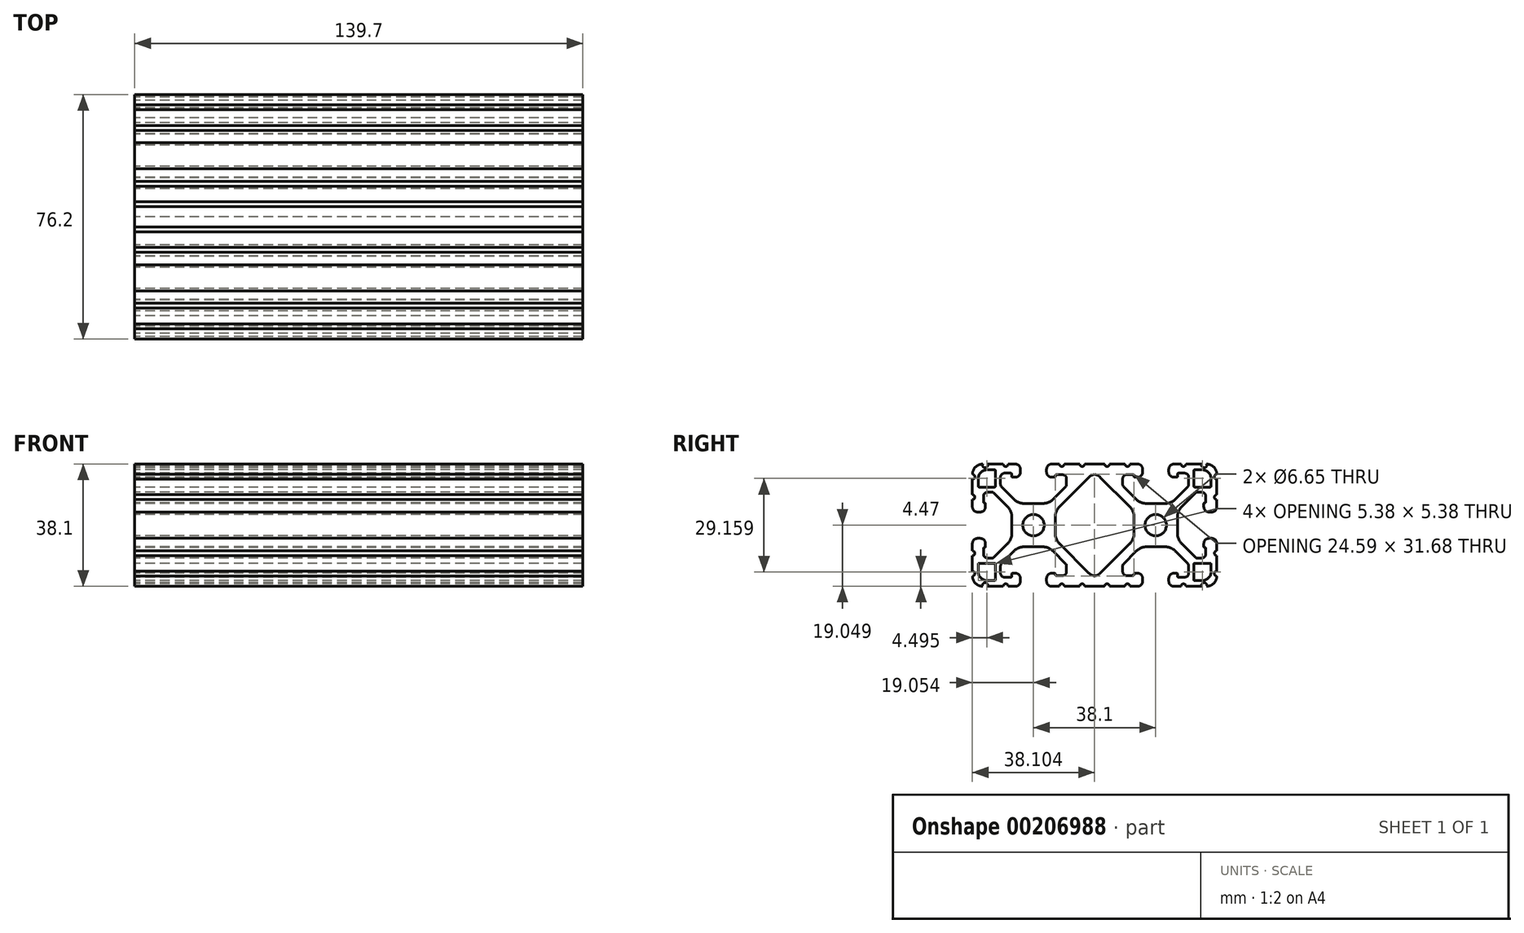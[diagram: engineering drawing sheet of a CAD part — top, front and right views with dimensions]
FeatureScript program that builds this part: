
annotation { "Feature Type Name" : "Feature", "Feature Type Description" : "" }
export const myFeature = defineFeature(function(context is Context, id is Id, definition is map)
    precondition{}
    {
        {
            var Q0;
            Q0=qCreatedBy(makeId("Right.planeOp"),FACE);
            var sketch = newSketch(context, id + "F0", { "sketchPlane" : qUnion([Q0])});
            skArc(sketch, "E0.0.0", {"start": v(-2.87, 19.05) * mm, "mid": v(-3.63, 18.29) * mm, "end": v(-4.4, 19.05) * mm});
            skLineSegment(sketch, "E0.0.1", {"start": v(-4.4, 19.05) * mm, "end": v(-9.22, 19.05) * mm});
            skArc(sketch, "E0.0.2", {"start": v(-9.22, 19.05) * mm, "mid": v(-9.98, 18.29) * mm, "end": v(-10.74, 19.05) * mm});
            skLineSegment(sketch, "E0.0.3", {"start": v(-10.74, 19.05) * mm, "end": v(-13.16, 19.05) * mm});
            skArc(sketch, "E0.0.4", {"start": v(-13.16, 19.05) * mm, "mid": v(-14.27, 18.59) * mm, "end": v(-14.73, 17.47) * mm});
            skLineSegment(sketch, "E0.0.5", {"start": v(-14.73, 17.47) * mm, "end": v(-14.73, 16.56) * mm});
            skArc(sketch, "E0.0.6", {"start": v(-14.73, 16.56) * mm, "mid": v(-14.27, 15.45) * mm, "end": v(-13.16, 14.99) * mm});
            skLineSegment(sketch, "E0.0.7", {"start": v(-13.16, 14.99) * mm, "end": v(-12.22, 14.99) * mm});
            skArc(sketch, "E0.0.8", {"start": v(-12.22, 14.99) * mm, "mid": v(-12.04, 15.06) * mm, "end": v(-11.96, 15.24) * mm});
            skLineSegment(sketch, "E0.0.9", {"start": v(-11.96, 15.24) * mm, "end": v(-11.96, 15.5) * mm});
            skArc(sketch, "E0.0.10", {"start": v(-11.96, 15.5) * mm, "mid": v(-11.89, 15.68) * mm, "end": v(-11.7, 15.75) * mm});
            skLineSegment(sketch, "E0.0.11", {"start": v(-11.7, 15.75) * mm, "end": v(-9.78, 15.75) * mm});
            skArc(sketch, "E0.0.12", {"start": v(-9.78, 15.75) * mm, "mid": v(-8.88, 15.38) * mm, "end": v(-8.5, 14.48) * mm});
            skLineSegment(sketch, "E0.0.13", {"start": v(-8.5, 14.48) * mm, "end": v(-8.5, 12.63) * mm});
            skArc(sketch, "E0.0.14", {"start": v(-8.5, 12.63) * mm, "mid": v(-8.58, 12.3) * mm, "end": v(-8.77, 12) * mm});
            skLineSegment(sketch, "E0.0.15", {"start": v(-8.77, 12) * mm, "end": v(-12.65, 8.12) * mm});
            skArc(sketch, "E0.0.16", {"start": v(-12.65, 8.12) * mm, "mid": v(-14.17, 7.11) * mm, "end": v(-15.95, 6.76) * mm});
            skLineSegment(sketch, "E0.0.17", {"start": v(-15.95, 6.76) * mm, "end": v(-21.69, 6.76) * mm});
            skArc(sketch, "E0.0.18", {"start": v(-21.69, 6.76) * mm, "mid": v(-23.43, 7.1) * mm, "end": v(-24.9, 8.09) * mm});
            skLineSegment(sketch, "E0.0.19", {"start": v(-24.9, 8.09) * mm, "end": v(-28.7, 11.9) * mm});
            skArc(sketch, "E0.0.20", {"start": v(-28.7, 11.9) * mm, "mid": v(-28.99, 12.3) * mm, "end": v(-29.08, 12.8) * mm});
            skLineSegment(sketch, "E0.0.21", {"start": v(-29.08, 12.8) * mm, "end": v(-29.08, 14.95) * mm});
            skArc(sketch, "E0.0.22", {"start": v(-29.08, 14.95) * mm, "mid": v(-28.71, 15.85) * mm, "end": v(-27.81, 16.22) * mm});
            skLineSegment(sketch, "E0.0.23", {"start": v(-27.81, 16.22) * mm, "end": v(-25.88, 16.22) * mm});
            skArc(sketch, "E0.0.24", {"start": v(-25.88, 16.22) * mm, "mid": v(-25.7, 16.14) * mm, "end": v(-25.63, 15.96) * mm});
            skLineSegment(sketch, "E0.0.25", {"start": v(-25.63, 15.96) * mm, "end": v(-25.63, 15.24) * mm});
            skArc(sketch, "E0.0.26", {"start": v(-25.63, 15.24) * mm, "mid": v(-25.56, 15.06) * mm, "end": v(-25.38, 14.99) * mm});
            skLineSegment(sketch, "E0.0.27", {"start": v(-25.38, 14.99) * mm, "end": v(-24.44, 14.99) * mm});
            skArc(sketch, "E0.0.28", {"start": v(-24.44, 14.99) * mm, "mid": v(-23.32, 15.45) * mm, "end": v(-22.86, 16.56) * mm});
            skLineSegment(sketch, "E0.0.29", {"start": v(-22.86, 16.56) * mm, "end": v(-22.86, 17.45) * mm});
            skArc(sketch, "E0.0.30", {"start": v(-22.86, 17.45) * mm, "mid": v(-23.33, 18.58) * mm, "end": v(-24.46, 19.05) * mm});
            skLineSegment(sketch, "E0.0.31", {"start": v(-24.46, 19.05) * mm, "end": v(-26.7, 19.05) * mm});
            skArc(sketch, "E0.0.32", {"start": v(-26.7, 19.05) * mm, "mid": v(-27.45, 18.29) * mm, "end": v(-28.22, 19.05) * mm});
            skLineSegment(sketch, "E0.0.33", {"start": v(-28.22, 19.05) * mm, "end": v(-33.15, 19.05) * mm});
            skArc(sketch, "E0.0.34", {"start": v(-33.15, 19.05) * mm, "mid": v(-33.9, 17.92) * mm, "end": v(-34.64, 19.05) * mm});
            skArc(sketch, "E0.0.35", {"start": v(-34.64, 19.05) * mm, "mid": v(-36.9, 18.11) * mm, "end": v(-37.82, 15.85) * mm});
            skArc(sketch, "E0.0.36", {"start": v(-37.82, 15.85) * mm, "mid": v(-37.07, 15.07) * mm, "end": v(-37.85, 14.32) * mm});
            skLineSegment(sketch, "E0.0.37", {"start": v(-37.85, 14.32) * mm, "end": v(-37.85, 9.5) * mm});
            skArc(sketch, "E0.0.38", {"start": v(-37.85, 9.5) * mm, "mid": v(-37.08, 8.73) * mm, "end": v(-37.85, 7.97) * mm});
            skLineSegment(sketch, "E0.0.39", {"start": v(-37.85, 7.97) * mm, "end": v(-37.85, 5.64) * mm});
            skArc(sketch, "E0.0.40", {"start": v(-37.85, 5.64) * mm, "mid": v(-37.4, 4.56) * mm, "end": v(-36.31, 4.11) * mm});
            skLineSegment(sketch, "E0.0.41", {"start": v(-36.31, 4.11) * mm, "end": v(-35.36, 4.11) * mm});
            skArc(sketch, "E0.0.42", {"start": v(-35.36, 4.11) * mm, "mid": v(-34.24, 4.57) * mm, "end": v(-33.78, 5.69) * mm});
            skLineSegment(sketch, "E0.0.43", {"start": v(-33.78, 5.69) * mm, "end": v(-33.78, 6.7) * mm});
            skArc(sketch, "E0.0.44", {"start": v(-33.78, 6.7) * mm, "mid": v(-33.86, 6.88) * mm, "end": v(-34.04, 6.96) * mm});
            skLineSegment(sketch, "E0.0.45", {"start": v(-34.04, 6.96) * mm, "end": v(-34.14, 6.96) * mm});
            skArc(sketch, "E0.0.46", {"start": v(-34.14, 6.96) * mm, "mid": v(-34.32, 7.03) * mm, "end": v(-34.4, 7.21) * mm});
            skLineSegment(sketch, "E0.0.47", {"start": v(-34.4, 7.21) * mm, "end": v(-34.4, 9.03) * mm});
            skArc(sketch, "E0.0.48", {"start": v(-34.4, 9.03) * mm, "mid": v(-34.02, 9.92) * mm, "end": v(-33.13, 10.3) * mm});
            skLineSegment(sketch, "E0.0.49", {"start": v(-33.13, 10.3) * mm, "end": v(-31.78, 10.3) * mm});
            skArc(sketch, "E0.0.50", {"start": v(-31.78, 10.3) * mm, "mid": v(-31.45, 10.22) * mm, "end": v(-31.17, 10.04) * mm});
            skLineSegment(sketch, "E0.0.51", {"start": v(-31.17, 10.04) * mm, "end": v(-26.94, 5.82) * mm});
            skArc(sketch, "E0.0.52", {"start": v(-26.94, 5.82) * mm, "mid": v(-25.91, 4.27) * mm, "end": v(-25.55, 2.46) * mm});
            skLineSegment(sketch, "E0.0.53", {"start": v(-25.55, 2.46) * mm, "end": v(-25.55, -2.46) * mm});
            skArc(sketch, "E0.0.54", {"start": v(-25.55, -2.46) * mm, "mid": v(-25.91, -4.28) * mm, "end": v(-26.94, -5.82) * mm});
            skLineSegment(sketch, "E0.0.55", {"start": v(-26.94, -5.82) * mm, "end": v(-31.17, -10.04) * mm});
            skArc(sketch, "E0.0.56", {"start": v(-31.17, -10.04) * mm, "mid": v(-31.45, -10.23) * mm, "end": v(-31.78, -10.3) * mm});
            skLineSegment(sketch, "E0.0.57", {"start": v(-31.78, -10.3) * mm, "end": v(-33.13, -10.3) * mm});
            skArc(sketch, "E0.0.58", {"start": v(-33.13, -10.3) * mm, "mid": v(-34.02, -9.92) * mm, "end": v(-34.4, -9.03) * mm});
            skLineSegment(sketch, "E0.0.59", {"start": v(-34.4, -9.03) * mm, "end": v(-34.4, -7.21) * mm});
            skArc(sketch, "E0.0.60", {"start": v(-34.4, -7.21) * mm, "mid": v(-34.32, -7.03) * mm, "end": v(-34.14, -6.96) * mm});
            skLineSegment(sketch, "E0.0.61", {"start": v(-34.14, -6.96) * mm, "end": v(-34.04, -6.96) * mm});
            skArc(sketch, "E0.0.62", {"start": v(-34.04, -6.96) * mm, "mid": v(-33.86, -6.89) * mm, "end": v(-33.78, -6.7) * mm});
            skLineSegment(sketch, "E0.0.63", {"start": v(-33.78, -6.7) * mm, "end": v(-33.78, -5.69) * mm});
            skArc(sketch, "E0.0.64", {"start": v(-33.78, -5.69) * mm, "mid": v(-34.24, -4.57) * mm, "end": v(-35.36, -4.11) * mm});
            skLineSegment(sketch, "E0.0.65", {"start": v(-35.36, -4.11) * mm, "end": v(-36.31, -4.11) * mm});
            skArc(sketch, "E0.0.66", {"start": v(-36.31, -4.11) * mm, "mid": v(-37.4, -4.56) * mm, "end": v(-37.85, -5.65) * mm});
            skLineSegment(sketch, "E0.0.67", {"start": v(-37.85, -5.65) * mm, "end": v(-37.85, -7.97) * mm});
            skArc(sketch, "E0.0.68", {"start": v(-37.85, -7.97) * mm, "mid": v(-37.08, -8.74) * mm, "end": v(-37.85, -9.5) * mm});
            skLineSegment(sketch, "E0.0.69", {"start": v(-37.85, -9.5) * mm, "end": v(-37.85, -14.33) * mm});
            skArc(sketch, "E0.0.70", {"start": v(-37.85, -14.33) * mm, "mid": v(-37.07, -15.08) * mm, "end": v(-37.82, -15.85) * mm});
            skArc(sketch, "E0.0.71", {"start": v(-37.82, -15.85) * mm, "mid": v(-36.9, -18.12) * mm, "end": v(-34.64, -19.05) * mm});
            skArc(sketch, "E0.0.72", {"start": v(-34.64, -19.05) * mm, "mid": v(-33.9, -17.92) * mm, "end": v(-33.15, -19.05) * mm});
            skLineSegment(sketch, "E0.0.73", {"start": v(-33.15, -19.05) * mm, "end": v(-28.22, -19.05) * mm});
            skArc(sketch, "E0.0.74", {"start": v(-28.22, -19.05) * mm, "mid": v(-27.45, -18.29) * mm, "end": v(-26.7, -19.05) * mm});
            skLineSegment(sketch, "E0.0.75", {"start": v(-26.7, -19.05) * mm, "end": v(-24.46, -19.05) * mm});
            skArc(sketch, "E0.0.76", {"start": v(-24.46, -19.05) * mm, "mid": v(-23.33, -18.58) * mm, "end": v(-22.86, -17.45) * mm});
            skLineSegment(sketch, "E0.0.77", {"start": v(-22.86, -17.45) * mm, "end": v(-22.86, -16.56) * mm});
            skArc(sketch, "E0.0.78", {"start": v(-22.86, -16.56) * mm, "mid": v(-23.32, -15.45) * mm, "end": v(-24.44, -14.99) * mm});
            skLineSegment(sketch, "E0.0.79", {"start": v(-24.44, -14.99) * mm, "end": v(-25.38, -14.99) * mm});
            skArc(sketch, "E0.0.80", {"start": v(-25.38, -14.99) * mm, "mid": v(-25.56, -15.06) * mm, "end": v(-25.63, -15.24) * mm});
            skLineSegment(sketch, "E0.0.81", {"start": v(-25.63, -15.24) * mm, "end": v(-25.63, -15.97) * mm});
            skArc(sketch, "E0.0.82", {"start": v(-25.63, -15.97) * mm, "mid": v(-25.7, -16.15) * mm, "end": v(-25.88, -16.22) * mm});
            skLineSegment(sketch, "E0.0.83", {"start": v(-25.88, -16.22) * mm, "end": v(-27.81, -16.22) * mm});
            skArc(sketch, "E0.0.84", {"start": v(-27.81, -16.22) * mm, "mid": v(-28.71, -15.85) * mm, "end": v(-29.08, -14.95) * mm});
            skLineSegment(sketch, "E0.0.85", {"start": v(-29.08, -14.95) * mm, "end": v(-29.08, -12.8) * mm});
            skArc(sketch, "E0.0.86", {"start": v(-29.08, -12.8) * mm, "mid": v(-28.99, -12.3) * mm, "end": v(-28.7, -11.9) * mm});
            skLineSegment(sketch, "E0.0.87", {"start": v(-28.7, -11.9) * mm, "end": v(-24.9, -8.1) * mm});
            skArc(sketch, "E0.0.88", {"start": v(-24.9, -8.1) * mm, "mid": v(-23.43, -7.1) * mm, "end": v(-21.69, -6.76) * mm});
            skLineSegment(sketch, "E0.0.89", {"start": v(-21.69, -6.76) * mm, "end": v(-15.95, -6.76) * mm});
            skArc(sketch, "E0.0.90", {"start": v(-15.95, -6.76) * mm, "mid": v(-14.17, -7.11) * mm, "end": v(-12.65, -8.13) * mm});
            skLineSegment(sketch, "E0.0.91", {"start": v(-12.65, -8.13) * mm, "end": v(-8.77, -12) * mm});
            skArc(sketch, "E0.0.92", {"start": v(-8.77, -12) * mm, "mid": v(-8.58, -12.3) * mm, "end": v(-8.5, -12.64) * mm});
            skLineSegment(sketch, "E0.0.93", {"start": v(-8.5, -12.64) * mm, "end": v(-8.5, -14.48) * mm});
            skArc(sketch, "E0.0.94", {"start": v(-8.5, -14.48) * mm, "mid": v(-8.88, -15.38) * mm, "end": v(-9.78, -15.75) * mm});
            skLineSegment(sketch, "E0.0.95", {"start": v(-9.78, -15.75) * mm, "end": v(-11.7, -15.75) * mm});
            skArc(sketch, "E0.0.96", {"start": v(-11.7, -15.75) * mm, "mid": v(-11.89, -15.68) * mm, "end": v(-11.96, -15.5) * mm});
            skLineSegment(sketch, "E0.0.97", {"start": v(-11.96, -15.5) * mm, "end": v(-11.96, -15.24) * mm});
            skArc(sketch, "E0.0.98", {"start": v(-11.96, -15.24) * mm, "mid": v(-12.04, -15.06) * mm, "end": v(-12.22, -14.99) * mm});
            skLineSegment(sketch, "E0.0.99", {"start": v(-12.22, -14.99) * mm, "end": v(-13.16, -14.99) * mm});
            skArc(sketch, "E0.0.100", {"start": v(-13.16, -14.99) * mm, "mid": v(-14.27, -15.45) * mm, "end": v(-14.73, -16.56) * mm});
            skLineSegment(sketch, "E0.0.101", {"start": v(-14.73, -16.56) * mm, "end": v(-14.73, -17.48) * mm});
            skArc(sketch, "E0.0.102", {"start": v(-14.73, -17.48) * mm, "mid": v(-14.27, -18.59) * mm, "end": v(-13.16, -19.05) * mm});
            skLineSegment(sketch, "E0.0.103", {"start": v(-13.16, -19.05) * mm, "end": v(-10.74, -19.05) * mm});
            skArc(sketch, "E0.0.104", {"start": v(-10.74, -19.05) * mm, "mid": v(-9.98, -18.29) * mm, "end": v(-9.22, -19.05) * mm});
            skLineSegment(sketch, "E0.0.105", {"start": v(-9.22, -19.05) * mm, "end": v(-4.4, -19.05) * mm});
            skArc(sketch, "E0.0.106", {"start": v(-4.4, -19.05) * mm, "mid": v(-3.63, -18.29) * mm, "end": v(-2.87, -19.05) * mm});
            skLineSegment(sketch, "E0.0.107", {"start": v(-2.87, -19.05) * mm, "end": v(3.38, -19.05) * mm});
            skArc(sketch, "E0.0.108", {"start": v(3.38, -19.05) * mm, "mid": v(4.14, -18.29) * mm, "end": v(4.9, -19.05) * mm});
            skLineSegment(sketch, "E0.0.109", {"start": v(4.9, -19.05) * mm, "end": v(9.73, -19.05) * mm});
            skArc(sketch, "E0.0.110", {"start": v(9.73, -19.05) * mm, "mid": v(10.49, -18.29) * mm, "end": v(11.25, -19.05) * mm});
            skLineSegment(sketch, "E0.0.111", {"start": v(11.25, -19.05) * mm, "end": v(13.66, -19.05) * mm});
            skArc(sketch, "E0.0.112", {"start": v(13.66, -19.05) * mm, "mid": v(14.78, -18.59) * mm, "end": v(15.24, -17.48) * mm});
            skLineSegment(sketch, "E0.0.113", {"start": v(15.24, -17.48) * mm, "end": v(15.24, -16.56) * mm});
            skArc(sketch, "E0.0.114", {"start": v(15.24, -16.56) * mm, "mid": v(14.78, -15.45) * mm, "end": v(13.66, -14.99) * mm});
            skLineSegment(sketch, "E0.0.115", {"start": v(13.66, -14.99) * mm, "end": v(12.72, -14.99) * mm});
            skArc(sketch, "E0.0.116", {"start": v(12.72, -14.99) * mm, "mid": v(12.54, -15.06) * mm, "end": v(12.47, -15.24) * mm});
            skLineSegment(sketch, "E0.0.117", {"start": v(12.47, -15.24) * mm, "end": v(12.47, -15.5) * mm});
            skArc(sketch, "E0.0.118", {"start": v(12.47, -15.5) * mm, "mid": v(12.4, -15.68) * mm, "end": v(12.22, -15.75) * mm});
            skLineSegment(sketch, "E0.0.119", {"start": v(12.22, -15.75) * mm, "end": v(10.29, -15.75) * mm});
            skArc(sketch, "E0.0.120", {"start": v(10.29, -15.75) * mm, "mid": v(9.39, -15.38) * mm, "end": v(9.02, -14.48) * mm});
            skLineSegment(sketch, "E0.0.121", {"start": v(9.02, -14.48) * mm, "end": v(9.02, -12.64) * mm});
            skArc(sketch, "E0.0.122", {"start": v(9.02, -12.64) * mm, "mid": v(9.08, -12.3) * mm, "end": v(9.28, -12) * mm});
            skLineSegment(sketch, "E0.0.123", {"start": v(9.28, -12) * mm, "end": v(13.16, -8.13) * mm});
            skArc(sketch, "E0.0.124", {"start": v(13.16, -8.13) * mm, "mid": v(14.67, -7.11) * mm, "end": v(16.46, -6.76) * mm});
            skLineSegment(sketch, "E0.0.125", {"start": v(16.46, -6.76) * mm, "end": v(22.2, -6.76) * mm});
            skArc(sketch, "E0.0.126", {"start": v(22.2, -6.76) * mm, "mid": v(23.94, -7.1) * mm, "end": v(25.42, -8.1) * mm});
            skLineSegment(sketch, "E0.0.127", {"start": v(25.42, -8.1) * mm, "end": v(29.22, -11.9) * mm});
            skArc(sketch, "E0.0.128", {"start": v(29.22, -11.9) * mm, "mid": v(29.5, -12.3) * mm, "end": v(29.6, -12.8) * mm});
            skLineSegment(sketch, "E0.0.129", {"start": v(29.6, -12.8) * mm, "end": v(29.6, -14.95) * mm});
            skArc(sketch, "E0.0.130", {"start": v(29.6, -14.95) * mm, "mid": v(29.22, -15.85) * mm, "end": v(28.32, -16.22) * mm});
            skLineSegment(sketch, "E0.0.131", {"start": v(28.32, -16.22) * mm, "end": v(26.4, -16.22) * mm});
            skArc(sketch, "E0.0.132", {"start": v(26.4, -16.22) * mm, "mid": v(26.21, -16.15) * mm, "end": v(26.14, -15.97) * mm});
            skLineSegment(sketch, "E0.0.133", {"start": v(26.14, -15.97) * mm, "end": v(26.14, -15.24) * mm});
            skArc(sketch, "E0.0.134", {"start": v(26.14, -15.24) * mm, "mid": v(26.06, -15.06) * mm, "end": v(25.88, -14.99) * mm});
            skLineSegment(sketch, "E0.0.135", {"start": v(25.88, -14.99) * mm, "end": v(24.94, -14.99) * mm});
            skArc(sketch, "E0.0.136", {"start": v(24.94, -14.99) * mm, "mid": v(23.83, -15.45) * mm, "end": v(23.37, -16.56) * mm});
            skLineSegment(sketch, "E0.0.137", {"start": v(23.37, -16.56) * mm, "end": v(23.37, -17.45) * mm});
            skArc(sketch, "E0.0.138", {"start": v(23.37, -17.45) * mm, "mid": v(23.84, -18.58) * mm, "end": v(24.97, -19.05) * mm});
            skLineSegment(sketch, "E0.0.139", {"start": v(24.97, -19.05) * mm, "end": v(27.2, -19.05) * mm});
            skArc(sketch, "E0.0.140", {"start": v(27.2, -19.05) * mm, "mid": v(27.96, -18.29) * mm, "end": v(28.72, -19.05) * mm});
            skLineSegment(sketch, "E0.0.141", {"start": v(28.72, -19.05) * mm, "end": v(33.65, -19.05) * mm});
            skArc(sketch, "E0.0.142", {"start": v(33.65, -19.05) * mm, "mid": v(34.4, -17.92) * mm, "end": v(35.15, -19.05) * mm});
            skArc(sketch, "E0.0.143", {"start": v(35.15, -19.05) * mm, "mid": v(37.4, -18.12) * mm, "end": v(38.33, -15.85) * mm});
            skArc(sketch, "E0.0.144", {"start": v(38.33, -15.85) * mm, "mid": v(37.58, -15.08) * mm, "end": v(38.35, -14.33) * mm});
            skLineSegment(sketch, "E0.0.145", {"start": v(38.35, -14.33) * mm, "end": v(38.35, -9.5) * mm});
            skArc(sketch, "E0.0.146", {"start": v(38.35, -9.5) * mm, "mid": v(37.6, -8.74) * mm, "end": v(38.35, -7.97) * mm});
            skLineSegment(sketch, "E0.0.147", {"start": v(38.35, -7.97) * mm, "end": v(38.35, -5.65) * mm});
            skArc(sketch, "E0.0.148", {"start": v(38.35, -5.65) * mm, "mid": v(37.9, -4.56) * mm, "end": v(36.82, -4.11) * mm});
            skLineSegment(sketch, "E0.0.149", {"start": v(36.82, -4.11) * mm, "end": v(35.86, -4.11) * mm});
            skArc(sketch, "E0.0.150", {"start": v(35.86, -4.11) * mm, "mid": v(34.75, -4.57) * mm, "end": v(34.29, -5.69) * mm});
            skLineSegment(sketch, "E0.0.151", {"start": v(34.29, -5.69) * mm, "end": v(34.29, -6.7) * mm});
            skArc(sketch, "E0.0.152", {"start": v(34.29, -6.7) * mm, "mid": v(34.36, -6.89) * mm, "end": v(34.54, -6.96) * mm});
            skLineSegment(sketch, "E0.0.153", {"start": v(34.54, -6.96) * mm, "end": v(34.65, -6.96) * mm});
            skArc(sketch, "E0.0.154", {"start": v(34.65, -6.96) * mm, "mid": v(34.83, -7.03) * mm, "end": v(34.9, -7.21) * mm});
            skLineSegment(sketch, "E0.0.155", {"start": v(34.9, -7.21) * mm, "end": v(34.9, -9.03) * mm});
            skArc(sketch, "E0.0.156", {"start": v(34.9, -9.03) * mm, "mid": v(34.53, -9.92) * mm, "end": v(33.64, -10.3) * mm});
            skLineSegment(sketch, "E0.0.157", {"start": v(33.64, -10.3) * mm, "end": v(32.29, -10.3) * mm});
            skArc(sketch, "E0.0.158", {"start": v(32.29, -10.3) * mm, "mid": v(31.95, -10.23) * mm, "end": v(31.67, -10.04) * mm});
            skLineSegment(sketch, "E0.0.159", {"start": v(31.67, -10.04) * mm, "end": v(27.45, -5.82) * mm});
            skArc(sketch, "E0.0.160", {"start": v(27.45, -5.82) * mm, "mid": v(26.42, -4.28) * mm, "end": v(26.06, -2.46) * mm});
            skLineSegment(sketch, "E0.0.161", {"start": v(26.06, -2.46) * mm, "end": v(26.06, 2.46) * mm});
            skArc(sketch, "E0.0.162", {"start": v(26.06, 2.46) * mm, "mid": v(26.42, 4.27) * mm, "end": v(27.45, 5.82) * mm});
            skLineSegment(sketch, "E0.0.163", {"start": v(27.45, 5.82) * mm, "end": v(31.67, 10.04) * mm});
            skArc(sketch, "E0.0.164", {"start": v(31.67, 10.04) * mm, "mid": v(31.95, 10.22) * mm, "end": v(32.29, 10.3) * mm});
            skLineSegment(sketch, "E0.0.165", {"start": v(32.29, 10.3) * mm, "end": v(33.64, 10.3) * mm});
            skArc(sketch, "E0.0.166", {"start": v(33.64, 10.3) * mm, "mid": v(34.53, 9.92) * mm, "end": v(34.9, 9.03) * mm});
            skLineSegment(sketch, "E0.0.167", {"start": v(34.9, 9.03) * mm, "end": v(34.9, 7.21) * mm});
            skArc(sketch, "E0.0.168", {"start": v(34.9, 7.21) * mm, "mid": v(34.83, 7.03) * mm, "end": v(34.65, 6.96) * mm});
            skLineSegment(sketch, "E0.0.169", {"start": v(34.65, 6.96) * mm, "end": v(34.54, 6.96) * mm});
            skArc(sketch, "E0.0.170", {"start": v(34.54, 6.96) * mm, "mid": v(34.36, 6.88) * mm, "end": v(34.29, 6.7) * mm});
            skLineSegment(sketch, "E0.0.171", {"start": v(34.29, 6.7) * mm, "end": v(34.29, 5.69) * mm});
            skArc(sketch, "E0.0.172", {"start": v(34.29, 5.69) * mm, "mid": v(34.75, 4.57) * mm, "end": v(35.86, 4.11) * mm});
            skLineSegment(sketch, "E0.0.173", {"start": v(35.86, 4.11) * mm, "end": v(36.82, 4.11) * mm});
            skArc(sketch, "E0.0.174", {"start": v(36.82, 4.11) * mm, "mid": v(37.9, 4.56) * mm, "end": v(38.35, 5.64) * mm});
            skLineSegment(sketch, "E0.0.175", {"start": v(38.35, 5.64) * mm, "end": v(38.35, 7.97) * mm});
            skArc(sketch, "E0.0.176", {"start": v(38.35, 7.97) * mm, "mid": v(37.6, 8.73) * mm, "end": v(38.35, 9.5) * mm});
            skLineSegment(sketch, "E0.0.177", {"start": v(38.35, 9.5) * mm, "end": v(38.35, 14.32) * mm});
            skArc(sketch, "E0.0.178", {"start": v(38.35, 14.32) * mm, "mid": v(37.58, 15.07) * mm, "end": v(38.33, 15.85) * mm});
            skArc(sketch, "E0.0.179", {"start": v(38.33, 15.85) * mm, "mid": v(37.4, 18.11) * mm, "end": v(35.15, 19.05) * mm});
            skArc(sketch, "E0.0.180", {"start": v(35.15, 19.05) * mm, "mid": v(34.4, 17.92) * mm, "end": v(33.65, 19.05) * mm});
            skLineSegment(sketch, "E0.0.181", {"start": v(33.65, 19.05) * mm, "end": v(28.72, 19.05) * mm});
            skArc(sketch, "E0.0.182", {"start": v(28.72, 19.05) * mm, "mid": v(27.96, 18.29) * mm, "end": v(27.2, 19.05) * mm});
            skLineSegment(sketch, "E0.0.183", {"start": v(27.2, 19.05) * mm, "end": v(24.97, 19.05) * mm});
            skArc(sketch, "E0.0.184", {"start": v(24.97, 19.05) * mm, "mid": v(23.84, 18.58) * mm, "end": v(23.37, 17.45) * mm});
            skLineSegment(sketch, "E0.0.185", {"start": v(23.37, 17.45) * mm, "end": v(23.37, 16.56) * mm});
            skArc(sketch, "E0.0.186", {"start": v(23.37, 16.56) * mm, "mid": v(23.83, 15.45) * mm, "end": v(24.94, 14.99) * mm});
            skLineSegment(sketch, "E0.0.187", {"start": v(24.94, 14.99) * mm, "end": v(25.88, 14.99) * mm});
            skArc(sketch, "E0.0.188", {"start": v(25.88, 14.99) * mm, "mid": v(26.06, 15.06) * mm, "end": v(26.14, 15.24) * mm});
            skLineSegment(sketch, "E0.0.189", {"start": v(26.14, 15.24) * mm, "end": v(26.14, 15.96) * mm});
            skArc(sketch, "E0.0.190", {"start": v(26.14, 15.96) * mm, "mid": v(26.21, 16.14) * mm, "end": v(26.4, 16.22) * mm});
            skLineSegment(sketch, "E0.0.191", {"start": v(26.4, 16.22) * mm, "end": v(28.32, 16.22) * mm});
            skArc(sketch, "E0.0.192", {"start": v(28.32, 16.22) * mm, "mid": v(29.22, 15.85) * mm, "end": v(29.6, 14.95) * mm});
            skLineSegment(sketch, "E0.0.193", {"start": v(29.6, 14.95) * mm, "end": v(29.6, 12.8) * mm});
            skArc(sketch, "E0.0.194", {"start": v(29.6, 12.8) * mm, "mid": v(29.5, 12.3) * mm, "end": v(29.22, 11.9) * mm});
            skLineSegment(sketch, "E0.0.195", {"start": v(29.22, 11.9) * mm, "end": v(25.42, 8.09) * mm});
            skArc(sketch, "E0.0.196", {"start": v(25.42, 8.09) * mm, "mid": v(23.94, 7.1) * mm, "end": v(22.2, 6.76) * mm});
            skLineSegment(sketch, "E0.0.197", {"start": v(22.2, 6.76) * mm, "end": v(16.46, 6.76) * mm});
            skArc(sketch, "E0.0.198", {"start": v(16.46, 6.76) * mm, "mid": v(14.67, 7.11) * mm, "end": v(13.16, 8.12) * mm});
            skLineSegment(sketch, "E0.0.199", {"start": v(13.16, 8.12) * mm, "end": v(9.28, 12) * mm});
            skArc(sketch, "E0.0.200", {"start": v(9.28, 12) * mm, "mid": v(9.08, 12.3) * mm, "end": v(9.02, 12.63) * mm});
            skLineSegment(sketch, "E0.0.201", {"start": v(9.02, 12.63) * mm, "end": v(9.02, 14.48) * mm});
            skArc(sketch, "E0.0.202", {"start": v(9.02, 14.48) * mm, "mid": v(9.39, 15.38) * mm, "end": v(10.29, 15.75) * mm});
            skLineSegment(sketch, "E0.0.203", {"start": v(10.29, 15.75) * mm, "end": v(12.22, 15.75) * mm});
            skArc(sketch, "E0.0.204", {"start": v(12.22, 15.75) * mm, "mid": v(12.4, 15.68) * mm, "end": v(12.47, 15.5) * mm});
            skLineSegment(sketch, "E0.0.205", {"start": v(12.47, 15.5) * mm, "end": v(12.47, 15.24) * mm});
            skArc(sketch, "E0.0.206", {"start": v(12.47, 15.24) * mm, "mid": v(12.54, 15.06) * mm, "end": v(12.72, 14.99) * mm});
            skLineSegment(sketch, "E0.0.207", {"start": v(12.72, 14.99) * mm, "end": v(13.66, 14.99) * mm});
            skArc(sketch, "E0.0.208", {"start": v(13.66, 14.99) * mm, "mid": v(14.78, 15.45) * mm, "end": v(15.24, 16.56) * mm});
            skLineSegment(sketch, "E0.0.209", {"start": v(15.24, 16.56) * mm, "end": v(15.24, 17.47) * mm});
            skArc(sketch, "E0.0.210", {"start": v(15.24, 17.47) * mm, "mid": v(14.78, 18.59) * mm, "end": v(13.66, 19.05) * mm});
            skLineSegment(sketch, "E0.0.211", {"start": v(13.66, 19.05) * mm, "end": v(11.25, 19.05) * mm});
            skArc(sketch, "E0.0.212", {"start": v(11.25, 19.05) * mm, "mid": v(10.49, 18.29) * mm, "end": v(9.73, 19.05) * mm});
            skLineSegment(sketch, "E0.0.213", {"start": v(9.73, 19.05) * mm, "end": v(4.9, 19.05) * mm});
            skArc(sketch, "E0.0.214", {"start": v(4.9, 19.05) * mm, "mid": v(4.14, 18.29) * mm, "end": v(3.38, 19.05) * mm});
            skLineSegment(sketch, "E0.0.215", {"start": v(3.38, 19.05) * mm, "end": v(-2.87, 19.05) * mm});
            skLineSegment(sketch, "E1.0", {"start": v(-30.66, 12.14) * mm, "end": v(-30.66, 17.02) * mm});
            skArc(sketch, "E1.1", {"start": v(-30.92, 11.89) * mm, "mid": v(-30.74, 11.96) * mm, "end": v(-30.66, 12.14) * mm});
            skLineSegment(sketch, "E1.2", {"start": v(-35.8, 11.89) * mm, "end": v(-30.92, 11.89) * mm});
            skLineSegment(sketch, "E1.4", {"start": v(-36.05, 14.48) * mm, "end": v(-36.05, 12.14) * mm});
            skPoint(sketch, "E1.5", {"position": v(-36.05, 12.14) * mm});
            skArc(sketch, "E1.6", {"start": v(-36.05, 12.14) * mm, "mid": v(-35.97, 11.96) * mm, "end": v(-35.8, 11.89) * mm});
            skArc(sketch, "E1.7", {"start": v(-33.25, 17.27) * mm, "mid": v(-35.23, 16.45) * mm, "end": v(-36.05, 14.48) * mm});
            skLineSegment(sketch, "E1.8", {"start": v(-30.92, 17.27) * mm, "end": v(-33.25, 17.27) * mm});
            skArc(sketch, "E1.9", {"start": v(-30.66, 17.02) * mm, "mid": v(-30.74, 17.2) * mm, "end": v(-30.92, 17.27) * mm});
            skCircle(sketch, "E1.10", {"center": v(-18.8, 0) * mm, "radius": 3.33 * mm});
            skLineSegment(sketch, "E1.11", {"start": v(-30.66, -17.02) * mm, "end": v(-30.66, -12.14) * mm});
            skArc(sketch, "E1.12", {"start": v(-30.92, -17.27) * mm, "mid": v(-30.74, -17.2) * mm, "end": v(-30.66, -17.02) * mm});
            skLineSegment(sketch, "E1.13", {"start": v(-33.25, -17.27) * mm, "end": v(-30.92, -17.27) * mm});
            skArc(sketch, "E1.14", {"start": v(-36.05, -14.48) * mm, "mid": v(-35.23, -16.45) * mm, "end": v(-33.25, -17.27) * mm});
            skLineSegment(sketch, "E1.15", {"start": v(-36.05, -12.14) * mm, "end": v(-36.05, -14.48) * mm});
            skArc(sketch, "E1.16", {"start": v(-35.8, -11.89) * mm, "mid": v(-35.97, -11.96) * mm, "end": v(-36.05, -12.14) * mm});
            skLineSegment(sketch, "E1.17", {"start": v(-30.92, -11.89) * mm, "end": v(-35.8, -11.89) * mm});
            skPoint(sketch, "E1.18", {"position": v(-30.92, -11.89) * mm});
            skArc(sketch, "E1.19", {"start": v(-30.66, -12.14) * mm, "mid": v(-30.74, -11.96) * mm, "end": v(-30.92, -11.89) * mm});
            skArc(sketch, "E2.0", {"start": v(0.25, -15.84) * mm, "mid": v(1.22, -15.53) * mm, "end": v(2.03, -14.94) * mm});
            skArc(sketch, "E2.1", {"start": v(-1.53, -14.94) * mm, "mid": v(-0.7, -15.53) * mm, "end": v(0.25, -15.84) * mm});
            skLineSegment(sketch, "E2.2", {"start": v(-10.65, -5.82) * mm, "end": v(-1.53, -14.94) * mm});
            skArc(sketch, "E2.3", {"start": v(-12.04, -2.46) * mm, "mid": v(-11.68, -4.28) * mm, "end": v(-10.65, -5.82) * mm});
            skLineSegment(sketch, "E2.4", {"start": v(-12.04, 2.46) * mm, "end": v(-12.04, -2.46) * mm});
            skArc(sketch, "E2.5", {"start": v(-10.65, 5.82) * mm, "mid": v(-11.68, 4.27) * mm, "end": v(-12.04, 2.46) * mm});
            skLineSegment(sketch, "E2.6", {"start": v(-1.53, 14.94) * mm, "end": v(-10.65, 5.82) * mm});
            skArc(sketch, "E2.7", {"start": v(0.25, 15.84) * mm, "mid": v(-0.7, 15.53) * mm, "end": v(-1.53, 14.94) * mm});
            skArc(sketch, "E2.8", {"start": v(2.03, 14.94) * mm, "mid": v(1.22, 15.53) * mm, "end": v(0.25, 15.84) * mm});
            skLineSegment(sketch, "E2.9", {"start": v(11.16, 5.82) * mm, "end": v(2.03, 14.94) * mm});
            skArc(sketch, "E2.10", {"start": v(12.55, 2.46) * mm, "mid": v(12.19, 4.27) * mm, "end": v(11.16, 5.82) * mm});
            skLineSegment(sketch, "E2.11", {"start": v(12.55, -2.46) * mm, "end": v(12.55, 2.46) * mm});
            skArc(sketch, "E2.12", {"start": v(11.16, -5.82) * mm, "mid": v(12.19, -4.28) * mm, "end": v(12.55, -2.46) * mm});
            skLineSegment(sketch, "E2.13", {"start": v(2.03, -14.94) * mm, "end": v(11.16, -5.82) * mm});
            skCircle(sketch, "E2.14", {"center": v(19.3, 0) * mm, "radius": 3.33 * mm});
            skLineSegment(sketch, "E2.15", {"start": v(36.56, -14.48) * mm, "end": v(36.56, -12.14) * mm});
            skArc(sketch, "E2.16", {"start": v(36.56, -12.14) * mm, "mid": v(36.48, -11.96) * mm, "end": v(36.3, -11.89) * mm});
            skLineSegment(sketch, "E2.17", {"start": v(36.3, -11.89) * mm, "end": v(31.42, -11.89) * mm});
            skArc(sketch, "E2.18", {"start": v(31.42, -11.89) * mm, "mid": v(31.24, -11.96) * mm, "end": v(31.17, -12.14) * mm});
            skLineSegment(sketch, "E2.19", {"start": v(31.17, -12.14) * mm, "end": v(31.17, -17.02) * mm});
            skArc(sketch, "E2.20", {"start": v(31.17, -17.02) * mm, "mid": v(31.24, -17.2) * mm, "end": v(31.42, -17.27) * mm});
            skLineSegment(sketch, "E2.21", {"start": v(31.42, -17.27) * mm, "end": v(33.76, -17.27) * mm});
            skArc(sketch, "E2.22", {"start": v(33.76, -17.27) * mm, "mid": v(35.74, -16.45) * mm, "end": v(36.56, -14.48) * mm});
            skLineSegment(sketch, "E2.23", {"start": v(31.42, 11.89) * mm, "end": v(36.3, 11.89) * mm});
            skArc(sketch, "E2.24", {"start": v(36.3, 11.89) * mm, "mid": v(36.48, 11.96) * mm, "end": v(36.56, 12.14) * mm});
            skLineSegment(sketch, "E2.25", {"start": v(36.56, 12.14) * mm, "end": v(36.56, 14.48) * mm});
            skArc(sketch, "E2.26", {"start": v(36.56, 14.48) * mm, "mid": v(35.74, 16.45) * mm, "end": v(33.76, 17.27) * mm});
            skLineSegment(sketch, "E2.27", {"start": v(33.76, 17.27) * mm, "end": v(31.42, 17.27) * mm});
            skArc(sketch, "E2.28", {"start": v(31.42, 17.27) * mm, "mid": v(31.24, 17.2) * mm, "end": v(31.17, 17.02) * mm});
            skLineSegment(sketch, "E2.29", {"start": v(31.17, 17.02) * mm, "end": v(31.17, 12.14) * mm});
            skArc(sketch, "E2.30", {"start": v(31.17, 12.14) * mm, "mid": v(31.24, 11.96) * mm, "end": v(31.42, 11.89) * mm});
            skSolve(sketch);
        }
        {
            var Q0;
            Q0 = qSketchRegion(id + "F0", true);
            extrude(context, id + "F1", {"entities" : qUnion([Q0]), "endBound" : BoundingType.SYMMETRIC, "depth" : 139.7 * mm});
        }
    });
